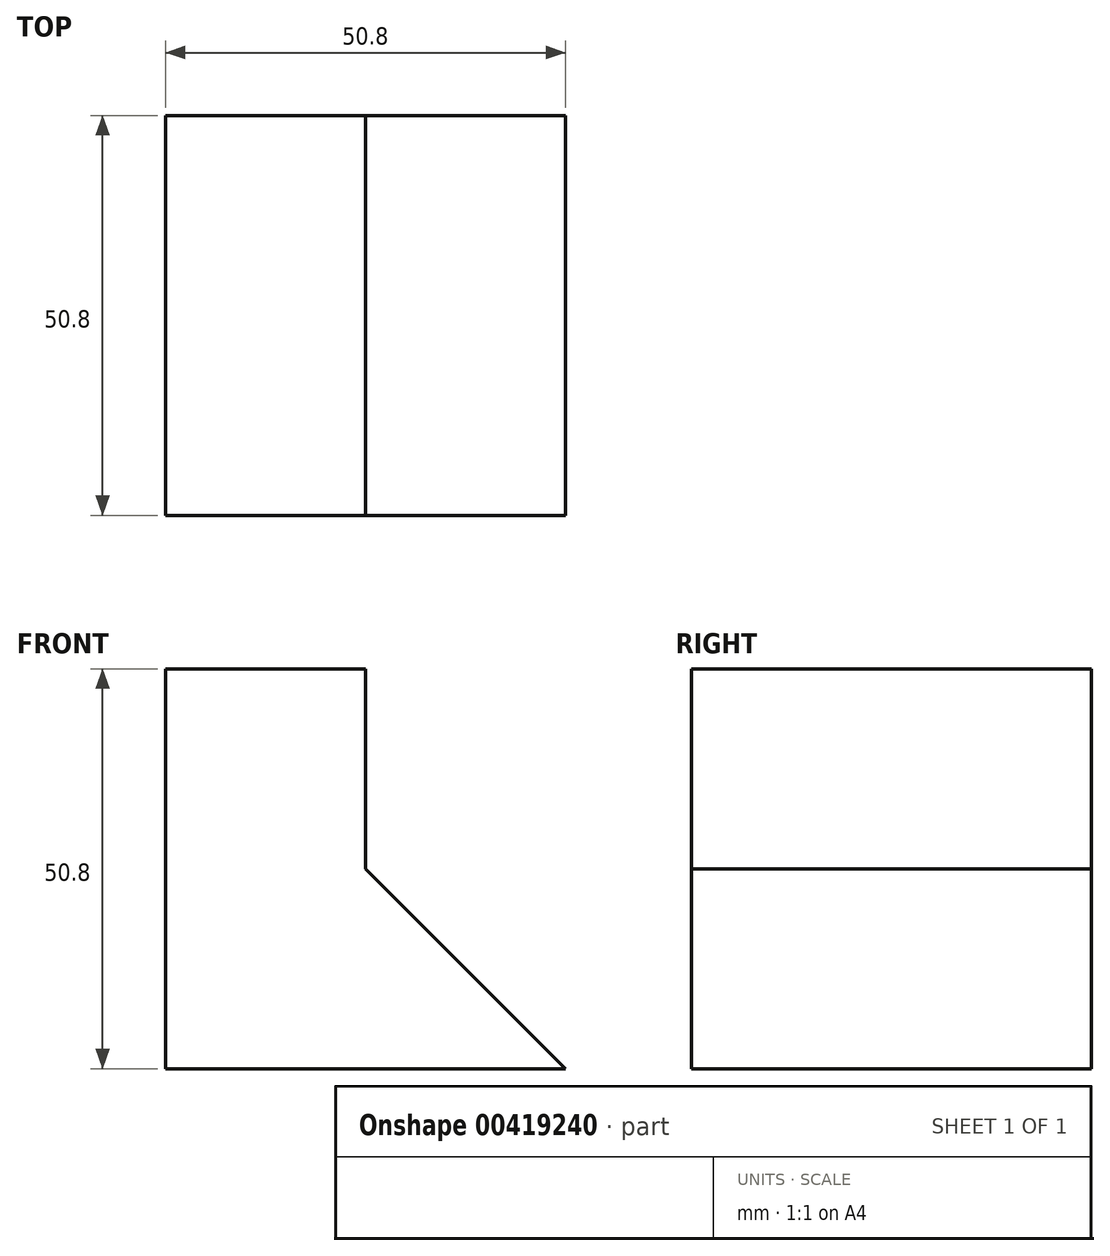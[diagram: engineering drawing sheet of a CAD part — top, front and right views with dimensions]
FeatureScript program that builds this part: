
annotation { "Feature Type Name" : "Feature", "Feature Type Description" : "" }
export const myFeature = defineFeature(function(context is Context, id is Id, definition is map)
    precondition{}
    {
        {
            var Q0;
            Q0=qCreatedBy(makeId("Front.planeOp"),FACE);
            var sketch = newSketch(context, id + "F0", { "sketchPlane" : qUnion([Q0])});
            skLineSegment(sketch, "E0", {"start": v(0, 0) * mm, "end": v(0, 50.8) * mm});
            skLineSegment(sketch, "E1", {"start": v(0, 50.8) * mm, "end": v(25.4, 50.8) * mm});
            skLineSegment(sketch, "E2", {"start": v(25.4, 50.8) * mm, "end": v(25.4, 25.4) * mm});
            skLineSegment(sketch, "E3", {"start": v(25.4, 25.4) * mm, "end": v(50.8, 0) * mm});
            skLineSegment(sketch, "E4", {"start": v(50.8, 0) * mm, "end": v(0, 0) * mm});
            skSolve(sketch);
        }
        {
            var Q0;
            Q0 = qSketchRegion(id + "F0", true);
            extrude(context, id + "F1", {"entities" : qUnion([Q0]), "depth" : 50.8 * mm});
        }
    });
